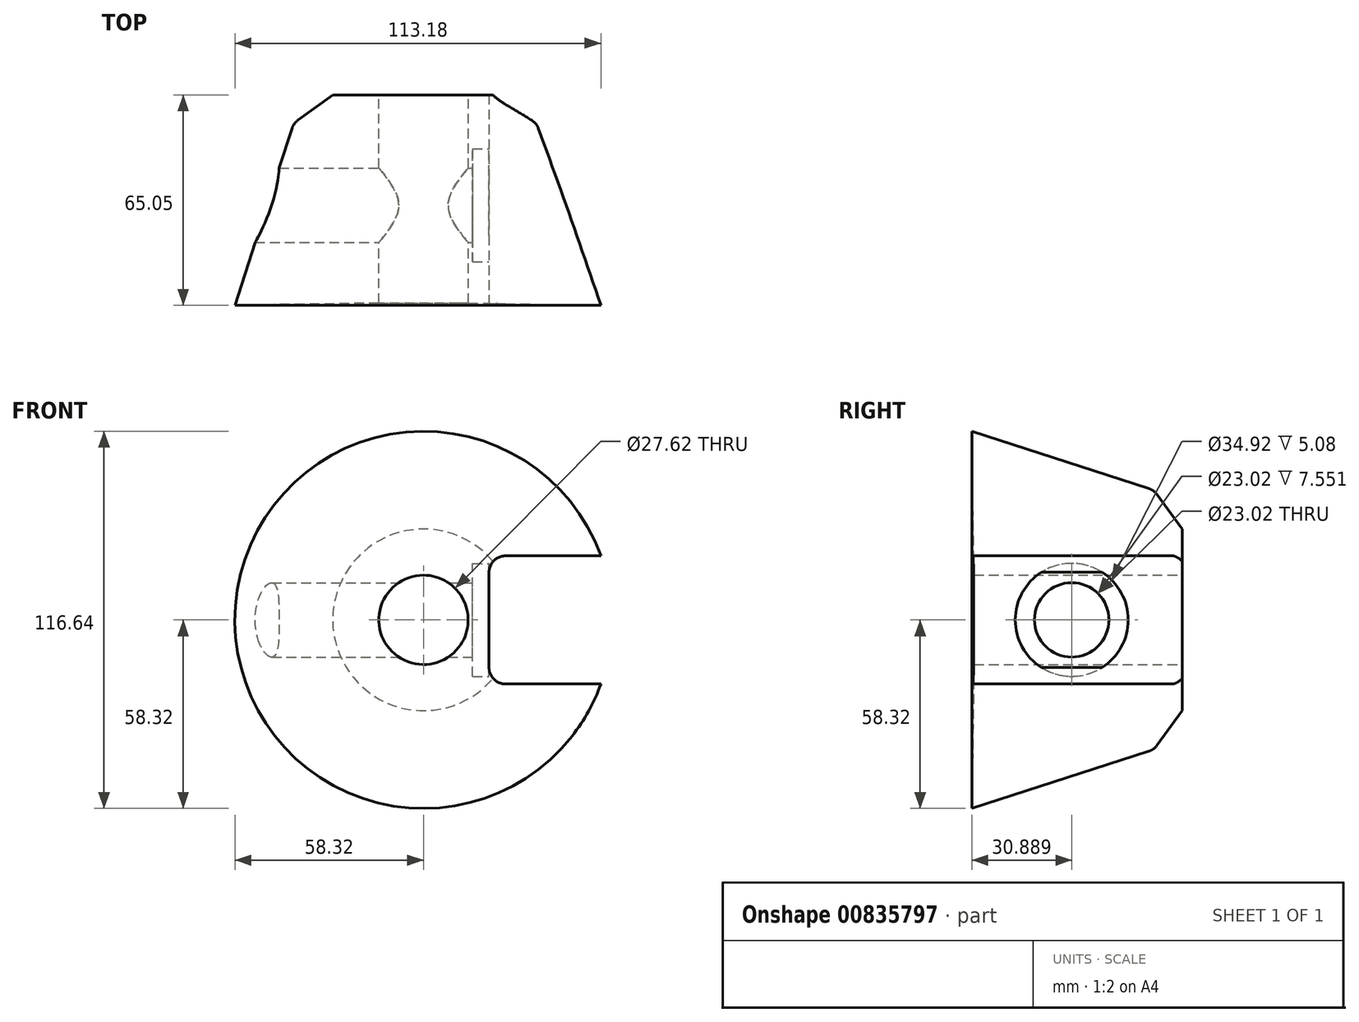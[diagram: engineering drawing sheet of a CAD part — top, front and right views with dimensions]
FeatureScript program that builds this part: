
annotation { "Feature Type Name" : "Feature", "Feature Type Description" : "" }
export const myFeature = defineFeature(function(context is Context, id is Id, definition is map)
    precondition{}
    {
        {
            var Q0;
            Q0=qCreatedBy(makeId("Top.planeOp"),FACE);
            var sketch = newSketch(context, id + "F0", { "sketchPlane" : qUnion([Q0])});
            skLineSegment(sketch, "E0", {"start": v(-58.32, -15.3) * mm, "end": v(-37.32, 49.76) * mm});
            skLineSegment(sketch, "E1", {"start": v(-37.32, 49.76) * mm, "end": v(-13.81, 49.76) * mm});
            skLineSegment(sketch, "E2", {"start": v(-13.81, 49.76) * mm, "end": v(-13.81, -14.6) * mm});
            skLineSegment(sketch, "E3", {"start": v(-13.81, -14.6) * mm, "end": v(-58.32, -15.3) * mm});
            skLineSegment(sketch, "E4", {"start": v(0, 0) * mm, "end": v(0, 45.65) * mm});
            skLineSegment(sketch, "E5", {"start": v(0, 45.65) * mm, "end": v(0, -24.65) * mm});
            skSolve(sketch);
        }
        {
            var Q0;
            Q0=makeQuery(id+"F0.imprint","IMPRINT",FACE,{"disambiguationData":[TD([[makeQuery(id+"F0.imprint","IMPRINT",EDGE,{"derivedFrom":sQuery(id+"F0.wireOp",EDGE,"E0")}),-1.0]])]});
            var Q1;
            Q1=sQuery(id+"F0.wireOp",EDGE,"E5");
            revolve(context, id + "F1", {"surfaceOperationType" : NewSurfaceOperationType.NEW, "entities" : qUnion([Q0]), "axis" : qUnion([Q1]), "revolveType" : RevolveType.FULL});
        }
        {
            var Q0;
            Q0=makeQuery(id+"F1.opRevolve","SWEPT_EDGE",EDGE,{"disambiguationData":[OSD([sQuery(id+"F0.wireOp",EDGE,"E0"),sQuery(id+"F0.wireOp",EDGE,"E1")])]});
            chamfer(context, id + "F2", {"entities" : qUnion([Q0]), "width" : 12.7 * mm, "tangentPropagation" : true});
        }
        {
            var Q0;
            {var subQ0=sQuery(id+"F0.wireOp",EDGE,"E0");Q0=makeQuery(id+"F2.opChamfer","BLEND_EDGE",EDGE,{"blendedFrom":[makeQuery(id+"F1.opRevolve","SWEPT_EDGE",EDGE,{"disambiguationData":[OSD([subQ0,sQuery(id+"F0.wireOp",EDGE,"E1")])]}),makeQuery(id+"F1.opRevolve","SWEPT_FACE",FACE,{"disambiguationData":[OSD([subQ0])]})],"blendedInto":[makeQuery(id+"F1.opRevolve","SWEPT_FACE",FACE,{"disambiguationData":[OSD([subQ0])]})]});}
            fillet(context, id + "F3", {"entities" : qUnion([Q0]), "radius" : 5.08 * mm, "tangentPropagation" : true, "allowEdgeOverflow" : false});
        }
        {
            var Q0;
            Q0=qCreatedBy(makeId("Top.planeOp"),FACE);
            var sketch = newSketch(context, id + "F4", { "sketchPlane" : qUnion([Q0])});
            skLineSegment(sketch, "E6.bottom", {"start": v(20.25, 53.39) * mm, "end": v(61.97, 53.39) * mm});
            skLineSegment(sketch, "E6.top", {"start": v(20.25, -37.78) * mm, "end": v(61.97, -37.78) * mm});
            skLineSegment(sketch, "E6.left", {"start": v(20.25, 53.39) * mm, "end": v(20.25, -37.78) * mm});
            skLineSegment(sketch, "E6.right", {"start": v(61.97, 53.39) * mm, "end": v(61.97, -37.78) * mm});
            skSolve(sketch);
        }
        {
            var Q0;
            Q0=makeQuery(id+"F4.imprint","IMPRINT",FACE,{"disambiguationData":[TD([[makeQuery(id+"F4.imprint","IMPRINT",EDGE,{"derivedFrom":sQuery(id+"F4.wireOp",EDGE,"E6.bottom")}),-1.0]])]});
            extrude(context, id + "F5", {"entities" : qUnion([Q0]), "operationType" : NewBodyOperationType.REMOVE, "endBound" : BoundingType.SYMMETRIC, "oppositeDirection" : true, "depth" : 39.62 * mm, "offsetDistance" : 25.4 * mm});
        }
        {
            var Q0;
            Q0=makeQuery(id+"F5.boolean.opBoolean","COPY",EDGE,{"derivedFrom":makeQuery(id+"F5.opExtrude","CAP_EDGE",EDGE,{"disambiguationData":[OSD([sQuery(id+"F4.wireOp",EDGE,"E6.left")])],"isStart":false})});
            var Q1;
            Q1=makeQuery(id+"F5.boolean.opBoolean","COPY",EDGE,{"derivedFrom":makeQuery(id+"F5.opExtrude","CAP_EDGE",EDGE,{"disambiguationData":[OSD([sQuery(id+"F4.wireOp",EDGE,"E6.left")])],"isStart":true})});
            fillet(context, id + "F6", {"entities" : qUnion([Q0, Q1]), "radius" : 5.08 * mm, "tangentPropagation" : true, "allowEdgeOverflow" : false});
        }
        {
            var Q0;
            Q0=makeQuery(id+"F5.boolean.opBoolean","COPY",FACE,{"derivedFrom":makeQuery(id+"F5.opExtrude","SWEPT_FACE",FACE,{"disambiguationData":[OSD([sQuery(id+"F4.wireOp",EDGE,"E6.left")])]})});
            var sketch = newSketch(context, id + "F7", { "sketchPlane" : qUnion([Q0])});
            skLineSegment(sketch, "E7", {"start": v(15.6, 0) * mm, "end": v(65.37, 0) * mm});
            skSolve(sketch);
        }
        {
            var Q0;
            Q0=sQuery(id+"F7.wireOp",VERTEX,"E7.start");
            var Q1;
            Q1=makeQuery(id+"F1.opRevolve","SWEPT_BODY",BODY,{"disambiguationData":[OSD([sQuery(id+"F0.wireOp",EDGE,"E0"),sQuery(id+"F0.wireOp",EDGE,"E1"),sQuery(id+"F0.wireOp",EDGE,"E2"),sQuery(id+"F0.wireOp",EDGE,"E3")])]});
            hole(context, id + "F8", {"style" : HoleStyle.C_BORE, "endStyle" : HoleEndStyle.THROUGH, "holeDiameter" : 23.02 * mm, "cBoreDiameter" : 34.92 * mm, "cBoreDepth" : 5.08 * mm, "majorDiameter" : 6.35 * mm, "isTappedThrough" : true, "tappedDepth" : 12.7 * mm, "tapClearance" : 3, "locations" : qUnion([Q0]), "scope" : qUnion([Q1])});
        }
    });
